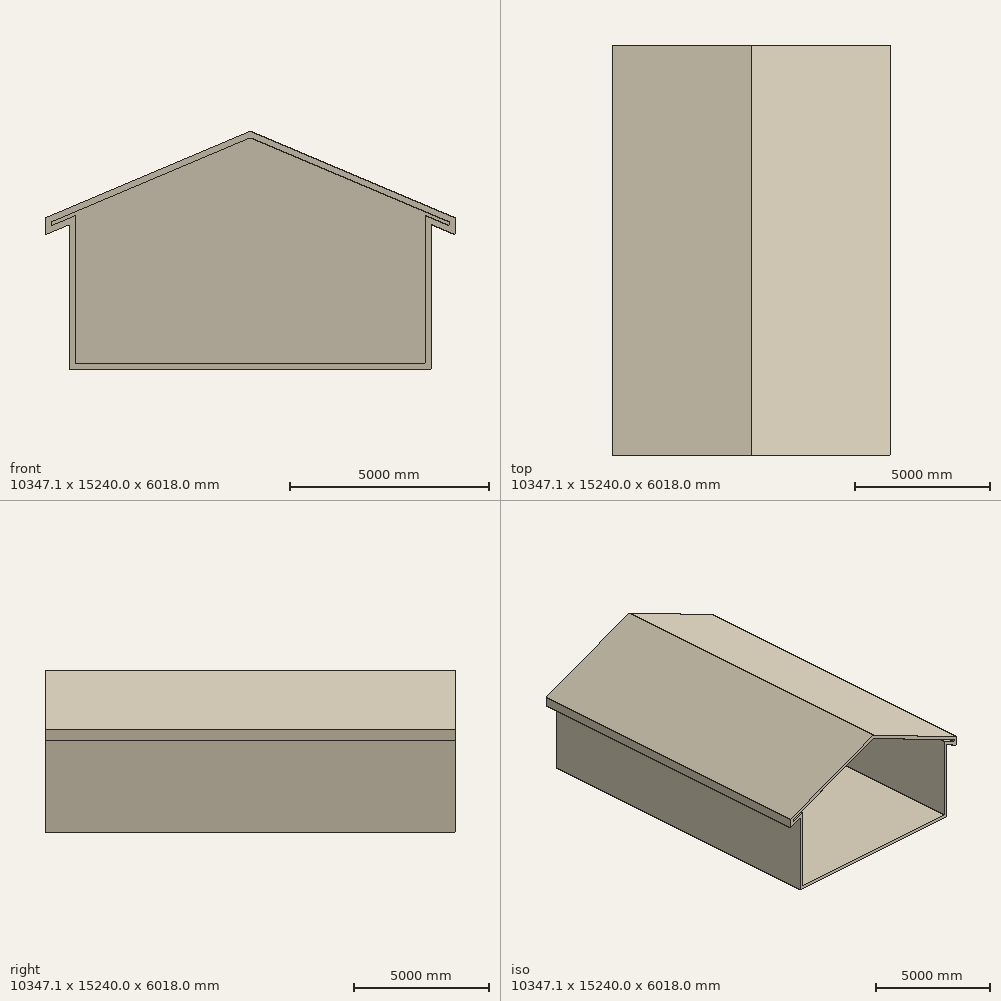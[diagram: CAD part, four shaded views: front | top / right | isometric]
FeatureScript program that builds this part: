
annotation { "Feature Type Name" : "Feature", "Feature Type Description" : "" }
export const myFeature = defineFeature(function(context is Context, id is Id, definition is map)
    precondition{}
    {
        {
            var Q0;
            Q0=qCreatedBy(makeId("Front.planeOp"),FACE);
            var sketch = newSketch(context, id + "F0", { "sketchPlane" : qUnion([Q0])});
            skLineSegment(sketch, "E0.bottom", {"start": v(0, 0) * mm, "end": v(9144, 0) * mm});
            skLineSegment(sketch, "E1", {"start": v(-602.1, 3400.37) * mm, "end": v(0, 3655.15) * mm});
            skLineSegment(sketch, "E2", {"start": v(9144, 3657.6) * mm, "end": v(9745.05, 3400.37) * mm});
            skLineSegment(sketch, "E3", {"start": v(0, 0) * mm, "end": v(0, 3655.15) * mm});
            skLineSegment(sketch, "E4", {"start": v(9144, 0) * mm, "end": v(9144, 3657.6) * mm});
            skLineSegment(sketch, "E5", {"start": v(-602.1, 3400.37) * mm, "end": v(-602.1, 3828.76) * mm});
            skLineSegment(sketch, "E6", {"start": v(-602.1, 3828.76) * mm, "end": v(4571.48, 6017.99) * mm});
            skLineSegment(sketch, "E7", {"start": v(4571.48, 6017.99) * mm, "end": v(9745.05, 3828.76) * mm});
            skLineSegment(sketch, "E8", {"start": v(9745.05, 3828.76) * mm, "end": v(9745.05, 3400.37) * mm});
            skSolve(sketch);
        }
        {
            var Q0;
            Q0=makeQuery(id+"F0.imprint","IMPRINT",FACE,{"disambiguationData":[TD([[makeQuery(id+"F0.imprint","IMPRINT",EDGE,{"derivedFrom":sQuery(id+"F0.wireOp",EDGE,"E0.bottom")}),1.0]])]});
            extrude(context, id + "F1", {"entities" : qUnion([Q0]), "oppositeDirection" : true, "depth" : 15240 * mm, "offsetDistance" : 25.4 * mm});
        }
        {
            var Q0;
            Q0=makeQuery(id+"F1.opExtrude","CAP_FACE",FACE,{"disambiguationData":[OSD([sQuery(id+"F0.wireOp",EDGE,"E0.bottom"),sQuery(id+"F0.wireOp",EDGE,"E0.left"),sQuery(id+"F0.wireOp",EDGE,"E0.right"),sQuery(id+"F0.wireOp",EDGE,"E1"),sQuery(id+"F0.wireOp",EDGE,"E2")])],"isStart":true});
            shell(context, id + "F2", {"entities" : qUnion([Q0]), "thickness" : 152.4 * mm});
        }
    });
